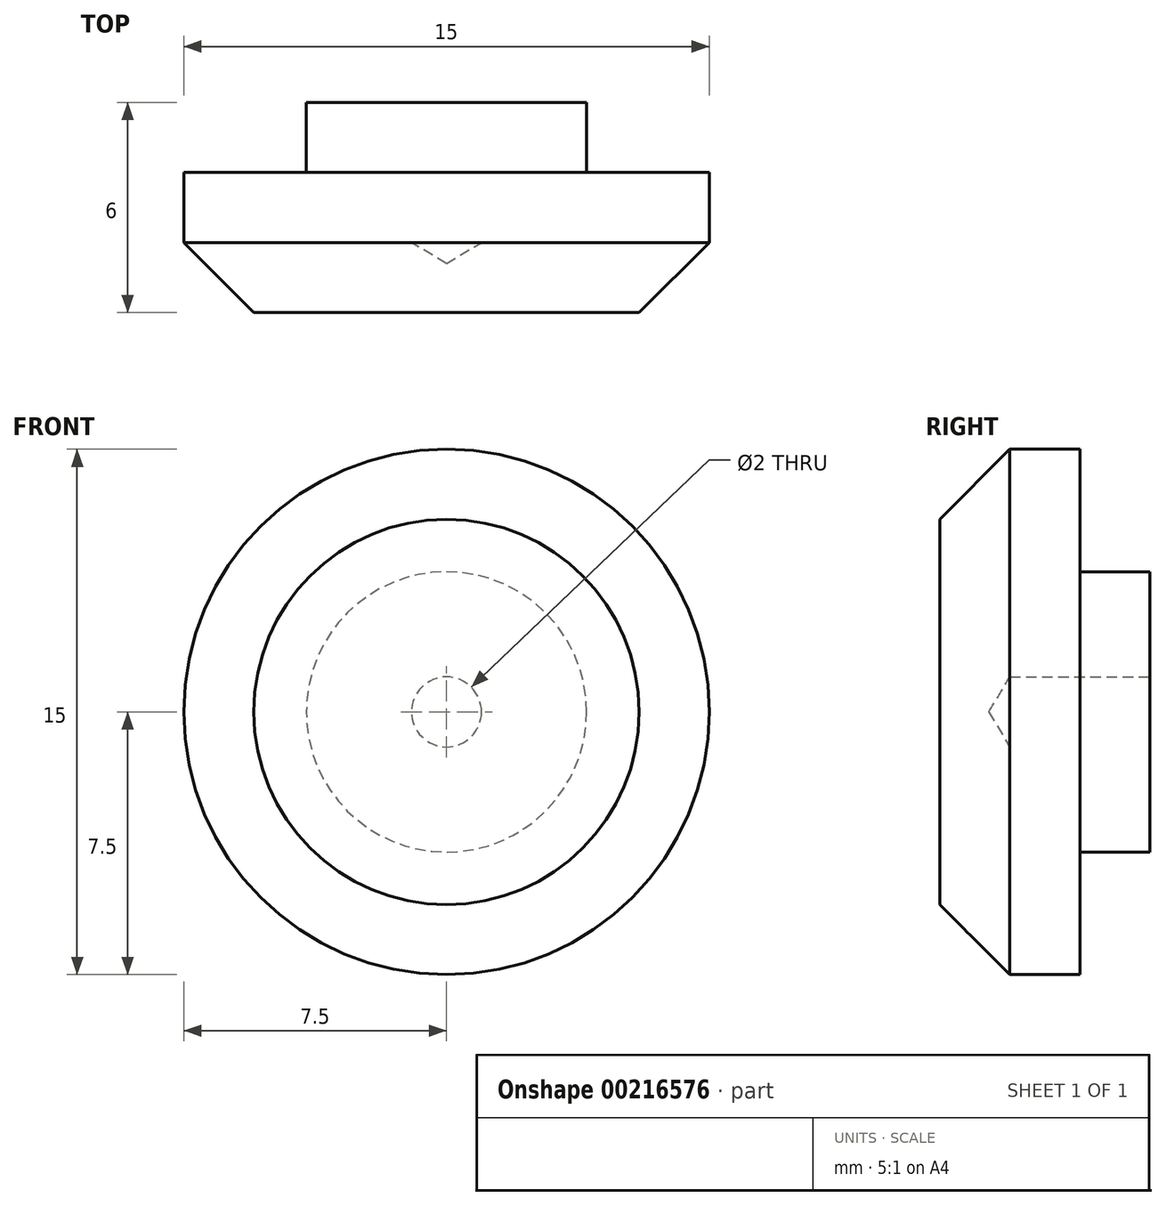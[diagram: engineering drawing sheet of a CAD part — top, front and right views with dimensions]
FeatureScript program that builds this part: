
annotation { "Feature Type Name" : "Feature", "Feature Type Description" : "" }
export const myFeature = defineFeature(function(context is Context, id is Id, definition is map)
    precondition{}
    {
        {
            var Q0;
            Q0=qCreatedBy(makeId("Front.planeOp"),FACE);
            var sketch = newSketch(context, id + "F0", { "sketchPlane" : qUnion([Q0])});
            skCircle(sketch, "E0", {"center": v(0, 0) * mm, "radius": 7.5 * mm});
            skSolve(sketch);
        }
        {
            var Q0;
            Q0 = qSketchRegion(id + "F0", true);
            extrude(context, id + "F1", {"entities" : qUnion([Q0]), "depth" : 4 * mm});
        }
        {
            var Q0;
            Q0=makeQuery(id+"F1.opExtrude","CAP_FACE",FACE,{"disambiguationData":[OSD([sQuery(id+"F0.wireOp",EDGE,"E0")])],"isStart":true});
            var sketch = newSketch(context, id + "F2", { "sketchPlane" : qUnion([Q0])});
            skCircle(sketch, "E1", {"center": v(0, 0) * mm, "radius": 4 * mm});
            skSolve(sketch);
        }
        {
            var Q0;
            Q0 = qSketchRegion(id + "F2", true);
            extrude(context, id + "F3", {"entities" : qUnion([Q0]), "operationType" : NewBodyOperationType.ADD, "depth" : 2 * mm});
        }
        {
            var Q0;
            Q0=makeQuery(id+"F3.opExtrude","CAP_FACE",FACE,{"disambiguationData":[OSD([sQuery(id+"F2.wireOp",EDGE,"E1")])],"isStart":false});
            var sketch = newSketch(context, id + "F4", { "sketchPlane" : qUnion([Q0])});
            skPoint(sketch, "E2", {"position": v(0, 0) * mm});
            skSolve(sketch);
        }
        {
            var Q0;
            Q0=sQuery(id+"F4.wireOp",VERTEX,"E2");
            var Q1;
            Q1=makeQuery(id+"F1.opExtrude","SWEPT_BODY",BODY,{"disambiguationData":[OSD([sQuery(id+"F0.wireOp",EDGE,"E0")])]});
            hole(context, id + "F5", {"style" : HoleStyle.SIMPLE, "endStyle" : HoleEndStyle.BLIND, "holeDiameter" : 2 * mm, "holeDepth" : 4 * mm, "locations" : qUnion([Q0]), "scope" : qUnion([Q1])});
        }
        {
            var Q0;
            Q0=makeQuery(id+"F1.opExtrude","CAP_EDGE",EDGE,{"disambiguationData":[OSD([sQuery(id+"F0.wireOp",EDGE,"E0")])],"isStart":false});
            chamfer(context, id + "F6", {"entities" : qUnion([Q0]), "width" : 2 * mm, "tangentPropagation" : true});
        }
    });
